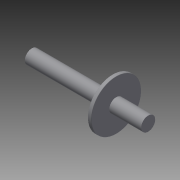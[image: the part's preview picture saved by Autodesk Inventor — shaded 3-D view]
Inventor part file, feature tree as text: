
AUTODESK INVENTOR PART (.ipt)
format: ipt  version: 2015 (Build 190159000, 159)  size: 97,792 bytes
history: native  units: in
note: dims shown in document units (in); Inventor stores cm internally (conversion verified against a paired STEP export)
features: revolve x1, fillet x1, sketch x1
ambient origin geometry x8: Origin, YZ Plane, XZ Plane, XY Plane, X Axis, Y Axis, Z Axis, Center Point
bodies: Solid1 (feature_tree)
feature tree (3):
  revolve  "Revolution1"  [1 undecoded]
  fillet  "Fillet1"  Radius=0.3937in
  sketch  "Sketch1"  dims[d0=0.1535in d1=0.5906in d2=0.3937in d3=0.0787in d4=0.3937in d5=0.5906in d6=1.1811in d7=90.0deg d8=0.0079in]
note: 1 required parameter value undecoded (feature->parameter linkage not recoverable at this tier; creation-order binding heuristic only, values carry confidence <= 0.55)
